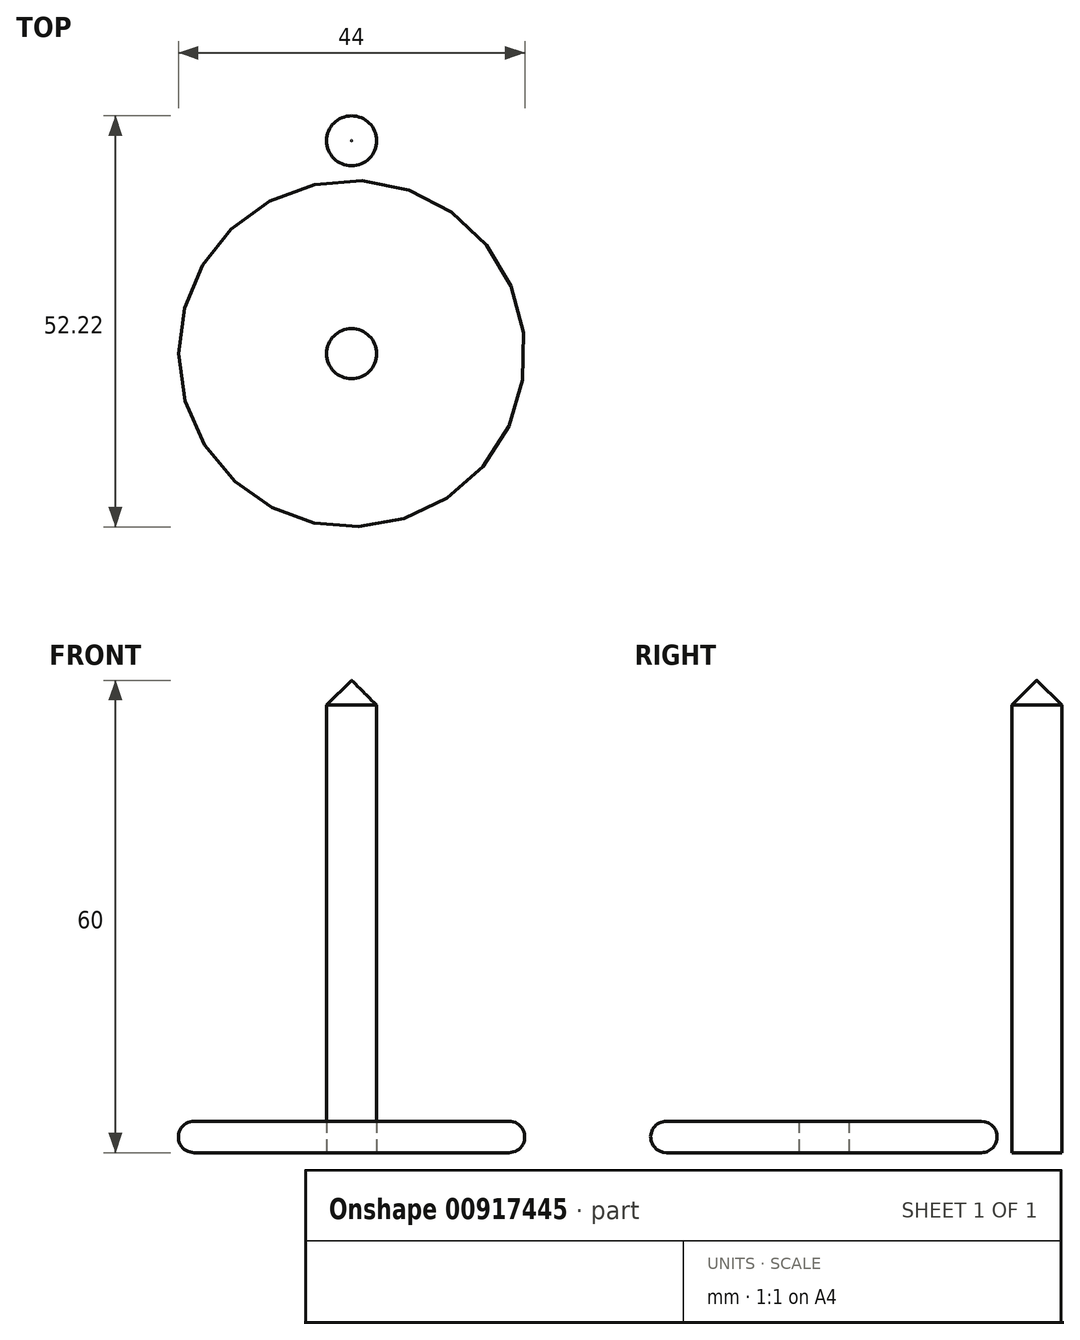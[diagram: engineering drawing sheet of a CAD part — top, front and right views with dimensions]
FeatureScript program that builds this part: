
annotation { "Feature Type Name" : "Feature", "Feature Type Description" : "" }
export const myFeature = defineFeature(function(context is Context, id is Id, definition is map)
    precondition{}
    {
        {
            var Q0;
            Q0=qCreatedBy(makeId("Front.planeOp"),FACE);
            var sketch = newSketch(context, id + "F0", { "sketchPlane" : qUnion([Q0])});
            skLineSegment(sketch, "E0.bottom", {"start": v(0, 0) * mm, "end": v(20, 0) * mm});
            skLineSegment(sketch, "E0.top", {"start": v(0, 4) * mm, "end": v(20, 4) * mm});
            skLineSegment(sketch, "E0.left", {"start": v(0, 0) * mm, "end": v(0, 4) * mm});
            skArc(sketch, "E1", {"start": v(20, 0) * mm, "mid": v(22, 2) * mm, "end": v(20, 4) * mm});
            skSolve(sketch);
        }
        {
            var Q0;
            Q0=qCreatedBy(makeId("Top.planeOp"),FACE);
            var sketch = newSketch(context, id + "F1", { "sketchPlane" : qUnion([Q0])});
            skCircle(sketch, "E2", {"center": v(0, 0) * mm, "radius": 3.18 * mm});
            skSolve(sketch);
        }
        {
            var Q0;
            {var subQ0=sQuery(id+"F0.wireOp",EDGE,"E0.right");Q0=makeQuery(id+"F0.imprint","IMPRINT",FACE,{"disambiguationData":[TD([[makeQuery(id+"F0.imprint","IMPRINT",EDGE,{"derivedFrom":subQ0}),-1.0]])]});}
            var Q1;
            {var subQ0=sQuery(id+"F0.wireOp",EDGE,"E0.bottom");Q1=makeQuery(id+"F0.imprint","IMPRINT",FACE,{"disambiguationData":[TD([[makeQuery(id+"F0.imprint","IMPRINT",EDGE,{"derivedFrom":subQ0}),1.0]])]});}
            var Q2;
            Q2=sQuery(id+"F0.wireOp",EDGE,"E0.left");
            revolve(context, id + "F2", {"surfaceOperationType" : NewSurfaceOperationType.NEW, "entities" : qUnion([Q0, Q1]), "axis" : qUnion([Q2]), "revolveType" : RevolveType.FULL});
        }
        {
            var Q0;
            Q0 = qSketchRegion(id + "F1", true);
            extrude(context, id + "F3", {"entities" : qUnion([Q0]), "operationType" : NewBodyOperationType.REMOVE, "depth" : 6 * mm, "offsetDistance" : 25 * mm});
        }
        {
            var Q0;
            Q0=qCreatedBy(makeId("Top.planeOp"),FACE);
            var sketch = newSketch(context, id + "F4", { "sketchPlane" : qUnion([Q0])});
            skCircle(sketch, "E3", {"center": v(0, 27.04) * mm, "radius": 3.17 * mm});
            skSolve(sketch);
        }
        {
            var Q0;
            Q0 = qSketchRegion(id + "F4", true);
            extrude(context, id + "F5", {"entities" : qUnion([Q0]), "depth" : 60 * mm, "offsetDistance" : 25 * mm});
        }
        {
            var Q0;
            Q0=makeQuery(id+"F5.opExtrude","CAP_EDGE",EDGE,{"disambiguationData":[OSD([sQuery(id+"F4.wireOp",EDGE,"E3")])],"isStart":false});
            chamfer(context, id + "F6", {"entities" : qUnion([Q0]), "width" : 3.15 * mm, "tangentPropagation" : true});
        }
    });
